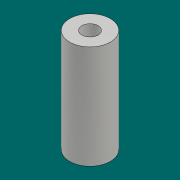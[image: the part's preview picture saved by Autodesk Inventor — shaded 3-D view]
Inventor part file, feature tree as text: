
AUTODESK INVENTOR PART (.ipt)
format: ipt  version: 2018 (Build 220112000, 112)  size: 78,848 bytes
history: native  units: mm
features: other x1, extrude x1, sketch x1
ambient origin geometry x8: Origin, YZ Plane, XZ Plane, XY Plane, X Axis, Y Axis, Z Axis, Center Point
bodies: Body1 (feature_tree)
feature tree (3):
  other  "ソリッド1"
  extrude  "押し出し1"  Depth=3.2mm
  sketch  "スケッチ1"
